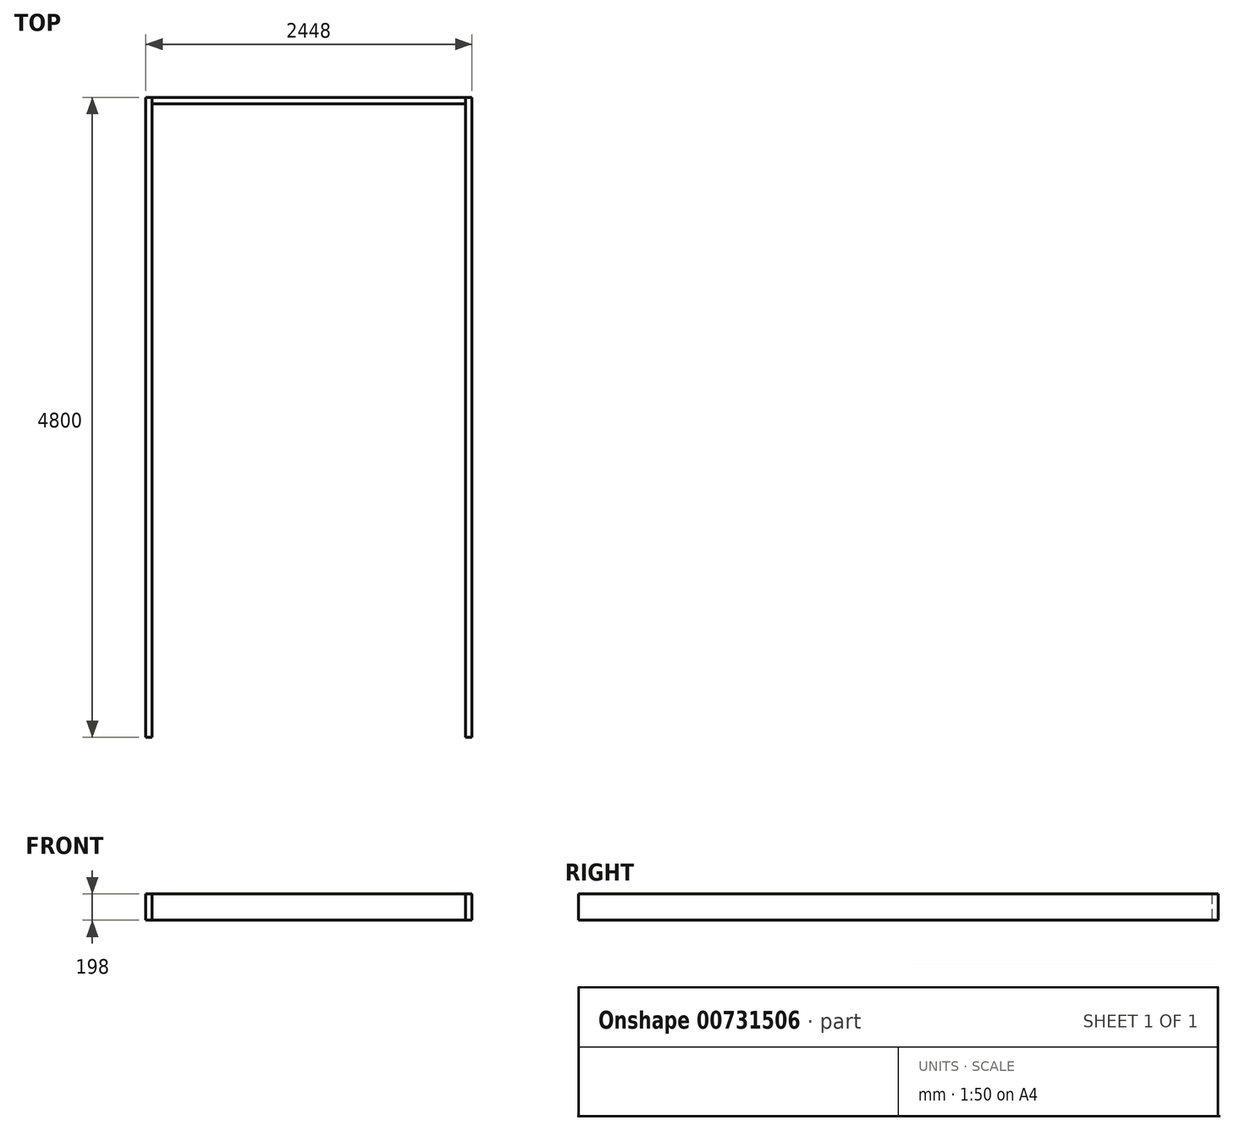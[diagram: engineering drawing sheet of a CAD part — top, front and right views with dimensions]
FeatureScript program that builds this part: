
annotation { "Feature Type Name" : "Feature", "Feature Type Description" : "" }
export const myFeature = defineFeature(function(context is Context, id is Id, definition is map)
    precondition{}
    {
        {
            var Q0;
            Q0=qCreatedBy(makeId("Top.planeOp"),FACE);
            var sketch = newSketch(context, id + "F0", { "sketchPlane" : qUnion([Q0])});
            skLineSegment(sketch, "E0.bottom", {"start": v(0, 0) * mm, "end": v(48, 0) * mm});
            skLineSegment(sketch, "E0.top", {"start": v(0, 4800) * mm, "end": v(48, 4800) * mm});
            skLineSegment(sketch, "E0.left", {"start": v(0, 0) * mm, "end": v(0, 4800) * mm});
            skLineSegment(sketch, "E0.right", {"start": v(48, 0) * mm, "end": v(48, 4800) * mm});
            skPoint(sketch, "E1.oppositeSnap0", {"position": v(24, 4800) * mm});
            skLineSegment(sketch, "E1.bottom", {"start": v(48, 4752) * mm, "end": v(2400, 4752) * mm});
            skLineSegment(sketch, "E1.top", {"start": v(48, 4800) * mm, "end": v(2400, 4800) * mm});
            skLineSegment(sketch, "E1.left", {"start": v(48, 4752) * mm, "end": v(48, 4800) * mm});
            skLineSegment(sketch, "E1.right", {"start": v(2400, 4752) * mm, "end": v(2400, 4800) * mm});
            skLineSegment(sketch, "E2.bottom", {"start": v(2400, 0) * mm, "end": v(2448, 0) * mm});
            skLineSegment(sketch, "E2.top", {"start": v(2400, 4800) * mm, "end": v(2448, 4800) * mm});
            skLineSegment(sketch, "E2.left", {"start": v(2400, 0) * mm, "end": v(2400, 4800) * mm});
            skLineSegment(sketch, "E2.right", {"start": v(2448, 0) * mm, "end": v(2448, 4800) * mm});
            skSolve(sketch);
        }
        {
            var Q0;
            Q0=makeQuery(id+"F0.imprint","IMPRINT",FACE,{"disambiguationData":[TD([[makeQuery(id+"F0.imprint","IMPRINT",EDGE,{"derivedFrom":sQuery(id+"F0.wireOp",EDGE,"E0.bottom")}),1.0]])]});
            extrude(context, id + "F1", {"entities" : qUnion([Q0]), "depth" : 198 * mm, "offsetDistance" : 25 * mm});
        }
        {
            var Q0;
            Q0=makeQuery(id+"F0.imprint","IMPRINT",FACE,{"disambiguationData":[TD([[makeQuery(id+"F0.imprint","IMPRINT",EDGE,{"derivedFrom":sQuery(id+"F0.wireOp",EDGE,"E1.bottom")}),1.0]])]});
            extrude(context, id + "F2", {"entities" : qUnion([Q0]), "depth" : 198 * mm, "offsetDistance" : 25 * mm});
        }
        {
            var Q0;
            {var subQ3=sQuery(id+"F0.wireOp",EDGE,"E2.bottom");Q0=makeQuery(id+"F0.imprint","IMPRINT",FACE,{"disambiguationData":[TD([[makeQuery(id+"F0.imprint","IMPRINT",EDGE,{"derivedFrom":subQ3}),1.0]])]});}
            extrude(context, id + "F3", {"entities" : qUnion([Q0]), "depth" : 198 * mm, "offsetDistance" : 25 * mm});
        }
    });
